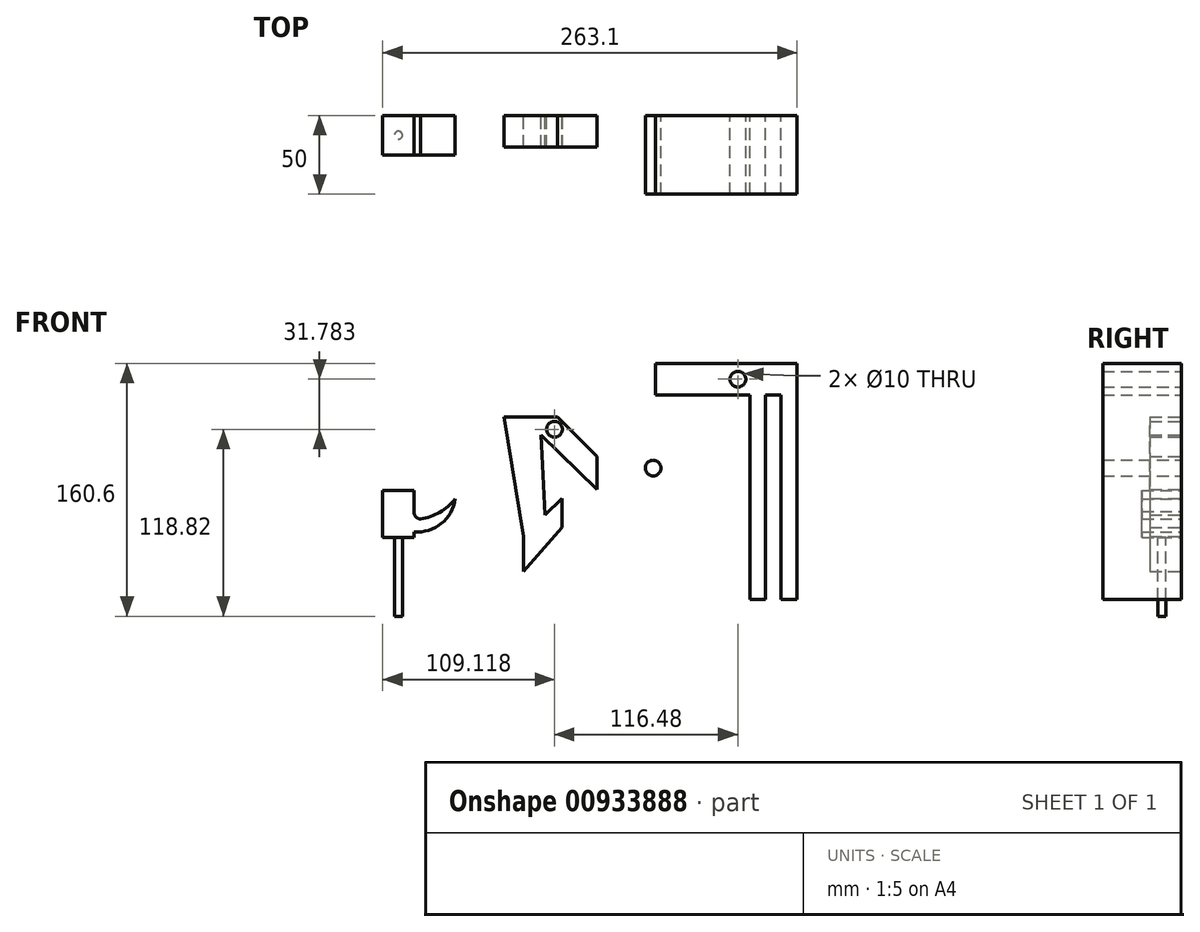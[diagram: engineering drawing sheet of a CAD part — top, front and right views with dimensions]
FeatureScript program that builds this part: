
annotation { "Feature Type Name" : "Feature", "Feature Type Description" : "" }
export const myFeature = defineFeature(function(context is Context, id is Id, definition is map)
    precondition{}
    {
        {
            var Q0;
            Q0=qCreatedBy(makeId("Front.planeOp"),FACE);
            var sketch = newSketch(context, id + "F0", { "sketchPlane" : qUnion([Q0])});
            skLineSegment(sketch, "E0", {"start": v(0, 18.59) * mm, "end": v(0, 0) * mm});
            skLineSegment(sketch, "E1", {"start": v(0, 0) * mm, "end": v(-24.18, -27.81) * mm});
            skLineSegment(sketch, "E2", {"start": v(0, 18.59) * mm, "end": v(-10.66, 7.87) * mm});
            skLineSegment(sketch, "E3", {"start": v(-24.18, -5.73) * mm, "end": v(-24.18, -27.81) * mm});
            skLineSegment(sketch, "E4", {"start": v(-2.66, 70.3) * mm, "end": v(22.5, 45.14) * mm});
            skLineSegment(sketch, "E5", {"start": v(22.5, 45.14) * mm, "end": v(22.5, 24.18) * mm});
            skLineSegment(sketch, "E6", {"start": v(22.5, 24.18) * mm, "end": v(-13.17, 58.94) * mm});
            skCircle(sketch, "E7", {"center": v(-4.61, 62.47) * mm, "radius": 5 * mm});
            skLineSegment(sketch, "E8", {"start": v(-2.66, 70.3) * mm, "end": v(-36.76, 70.3) * mm});
            skLineSegment(sketch, "E9", {"start": v(-13.17, 58.94) * mm, "end": v(-10.66, 7.87) * mm});
            skLineSegment(sketch, "E10", {"start": v(-36.76, 70.3) * mm, "end": v(-24.18, -5.73) * mm});
            skCircle(sketch, "E11", {"center": v(58.05, 37.8) * mm, "radius": 5 * mm});
            skLineSegment(sketch, "E12", {"start": v(119.37, -45.72) * mm, "end": v(119.37, 84.25) * mm});
            skLineSegment(sketch, "E13", {"start": v(119.37, 104.25) * mm, "end": v(149.37, 104.25) * mm});
            skLineSegment(sketch, "E14", {"start": v(149.37, 104.25) * mm, "end": v(149.37, -45.72) * mm});
            skLineSegment(sketch, "E15", {"start": v(149.37, -45.72) * mm, "end": v(139.37, -45.72) * mm});
            skLineSegment(sketch, "E16", {"start": v(139.37, -45.72) * mm, "end": v(139.37, 84.25) * mm});
            skLineSegment(sketch, "E17", {"start": v(139.37, 84.25) * mm, "end": v(129.37, 84.25) * mm});
            skLineSegment(sketch, "E18", {"start": v(129.37, 84.25) * mm, "end": v(129.37, -45.72) * mm});
            skLineSegment(sketch, "E19", {"start": v(129.37, -45.72) * mm, "end": v(119.37, -45.72) * mm});
            skLineSegment(sketch, "E20", {"start": v(119.37, 84.25) * mm, "end": v(59.37, 84.25) * mm});
            skLineSegment(sketch, "E21", {"start": v(59.37, 84.25) * mm, "end": v(59.37, 104.25) * mm});
            skLineSegment(sketch, "E22", {"start": v(59.37, 104.25) * mm, "end": v(119.37, 104.25) * mm});
            skCircle(sketch, "E23", {"center": v(111.87, 94.25) * mm, "radius": 5 * mm});
            skPoint(sketch, "E23.centerSnap0", {"position": v(59.37, 94.25) * mm});
            skLineSegment(sketch, "E24", {"start": v(-93.73, 23.65) * mm, "end": v(-93.73, 13.43) * mm});
            skLineSegment(sketch, "E25", {"start": v(-93.73, -6.35) * mm, "end": v(-113.73, -6.35) * mm});
            skLineSegment(sketch, "E26", {"start": v(-113.73, -6.35) * mm, "end": v(-113.73, 23.65) * mm});
            skLineSegment(sketch, "E27", {"start": v(-113.73, 23.65) * mm, "end": v(-93.73, 23.65) * mm});
            skLineSegment(sketch, "E28", {"start": v(-89.26, 13.43) * mm, "end": v(-90, 12.64) * mm});
            skLineSegment(sketch, "E29.trimOffspring", {"start": v(-93.73, -2.7) * mm, "end": v(-93.73, -6.35) * mm});
            skArc(sketch, "E30", {"start": v(-90, 12.64) * mm, "mid": v(-89.59, 13) * mm, "end": v(-89.26, 13.43) * mm});
            skPoint(sketch, "E30.startSnap0", {"position": v(-89.26, 13.43) * mm});
            skPoint(sketch, "E31.orphan", {"position": v(-93.73, 8.65) * mm});
            skArc(sketch, "E32", {"start": v(-93.73, -2.7) * mm, "mid": v(-76.55, 2.54) * mm, "end": v(-67.77, 18.2) * mm});
            skArc(sketch, "E33", {"start": v(-89.7, 5.47) * mm, "mid": v(-77.49, 9.69) * mm, "end": v(-67.77, 18.2) * mm});
            skLineSegment(sketch, "E34", {"start": v(-93.73, 13.43) * mm, "end": v(-93.73, 8.65) * mm});
            skPoint(sketch, "E35.orphan", {"position": v(-84.8, 18.2) * mm});
            skArc(sketch, "E36", {"start": v(-93.73, 10.26) * mm, "mid": v(-92.83, 6.93) * mm, "end": v(-89.7, 5.47) * mm});
            skPoint(sketch, "E37.orphan", {"position": v(-93.73, 5.16) * mm});
            skArc(sketch, "E38", {"start": v(260.59, 110) * mm, "mid": v(284.22, 24.64) * mm, "end": v(346.03, -38.8) * mm});
            skLineSegment(sketch, "E39", {"start": v(260.59, 110) * mm, "end": v(210.59, 110) * mm});
            skLineSegment(sketch, "E40", {"start": v(210.59, 110) * mm, "end": v(210.59, 196.2) * mm});
            skLineSegment(sketch, "E41", {"start": v(210.59, 196.2) * mm, "end": v(275.43, 196.2) * mm});
            skLineSegment(sketch, "E42", {"start": v(275.43, 196.2) * mm, "end": v(275.43, 211.2) * mm});
            skLineSegment(sketch, "E43", {"start": v(275.43, 211.2) * mm, "end": v(175.43, 211.2) * mm});
            skLineSegment(sketch, "E44", {"start": v(175.43, 211.2) * mm, "end": v(175.43, -38.8) * mm});
            skLineSegment(sketch, "E45", {"start": v(175.43, -38.8) * mm, "end": v(346.03, -38.8) * mm});
            skSolve(sketch);
        }
        {
            var Q0;
            Q0=makeQuery(id+"F0.imprint","IMPRINT",FACE,{"disambiguationData":[TD([[makeQuery(id+"F0.imprint","IMPRINT",EDGE,{"derivedFrom":sQuery(id+"F0.wireOp",EDGE,"E0")}),-1.0]])]});
            extrude(context, id + "F1", {"entities" : qUnion([Q0]), "depth" : 20 * mm, "offsetDistance" : 25 * mm});
        }
        {
            var Q0;
            Q0=makeQuery(id+"F0.imprint","IMPRINT",FACE,{"disambiguationData":[TD([[makeQuery(id+"F0.imprint","IMPRINT",EDGE,{"derivedFrom":sQuery(id+"F0.wireOp",EDGE,"E11")}),1.0]])]});
            extrude(context, id + "F2", {"entities" : qUnion([Q0]), "depth" : 50 * mm, "offsetDistance" : 25 * mm});
        }
        {
            var Q0;
            Q0=makeQuery(id+"F0.imprint","IMPRINT",FACE,{"disambiguationData":[TD([[makeQuery(id+"F0.imprint","IMPRINT",EDGE,{"derivedFrom":sQuery(id+"F0.wireOp",EDGE,"E12")}),-1.0]])]});
            extrude(context, id + "F3", {"entities" : qUnion([Q0]), "depth" : 50 * mm, "offsetDistance" : 25 * mm});
        }
        {
            var Q0;
            {var subQ0=sQuery(id+"F0.wireOp",EDGE,"E24");Q0=makeQuery(id+"F0.imprint","IMPRINT",FACE,{"disambiguationData":[TD([[makeQuery(id+"F0.imprint","IMPRINT",EDGE,{"derivedFrom":subQ0}),-1.0]])]});}
            extrude(context, id + "F4", {"entities" : qUnion([Q0]), "depth" : 25 * mm, "offsetDistance" : 25 * mm});
        }
        {
            var Q0;
            Q0=makeQuery(id+"F4.opExtrude","SWEPT_FACE",FACE,{"disambiguationData":[OSD([sQuery(id+"F0.wireOp",EDGE,"E25")])]});
            var sketch = newSketch(context, id + "F5", { "sketchPlane" : qUnion([Q0])});
            skCircle(sketch, "E46", {"center": v(-103.73, 12.5) * mm, "radius": 2.5 * mm});
            skPoint(sketch, "E46.centerSnap0", {"position": v(-113.73, 12.5) * mm});
            skPoint(sketch, "E46.centerSnap1", {"position": v(-103.73, 25) * mm});
            skSolve(sketch);
        }
        {
            var Q0;
            Q0=makeQuery(id+"F5.imprint","IMPRINT",FACE,{"disambiguationData":[TD([[makeQuery(id+"F5.imprint","IMPRINT",EDGE,{"derivedFrom":sQuery(id+"F5.wireOp",EDGE,"E46")}),1.0]])]});
            extrude(context, id + "F6", {"entities" : qUnion([Q0]), "operationType" : NewBodyOperationType.ADD, "depth" : 50 * mm, "offsetDistance" : 25 * mm});
        }
    });
